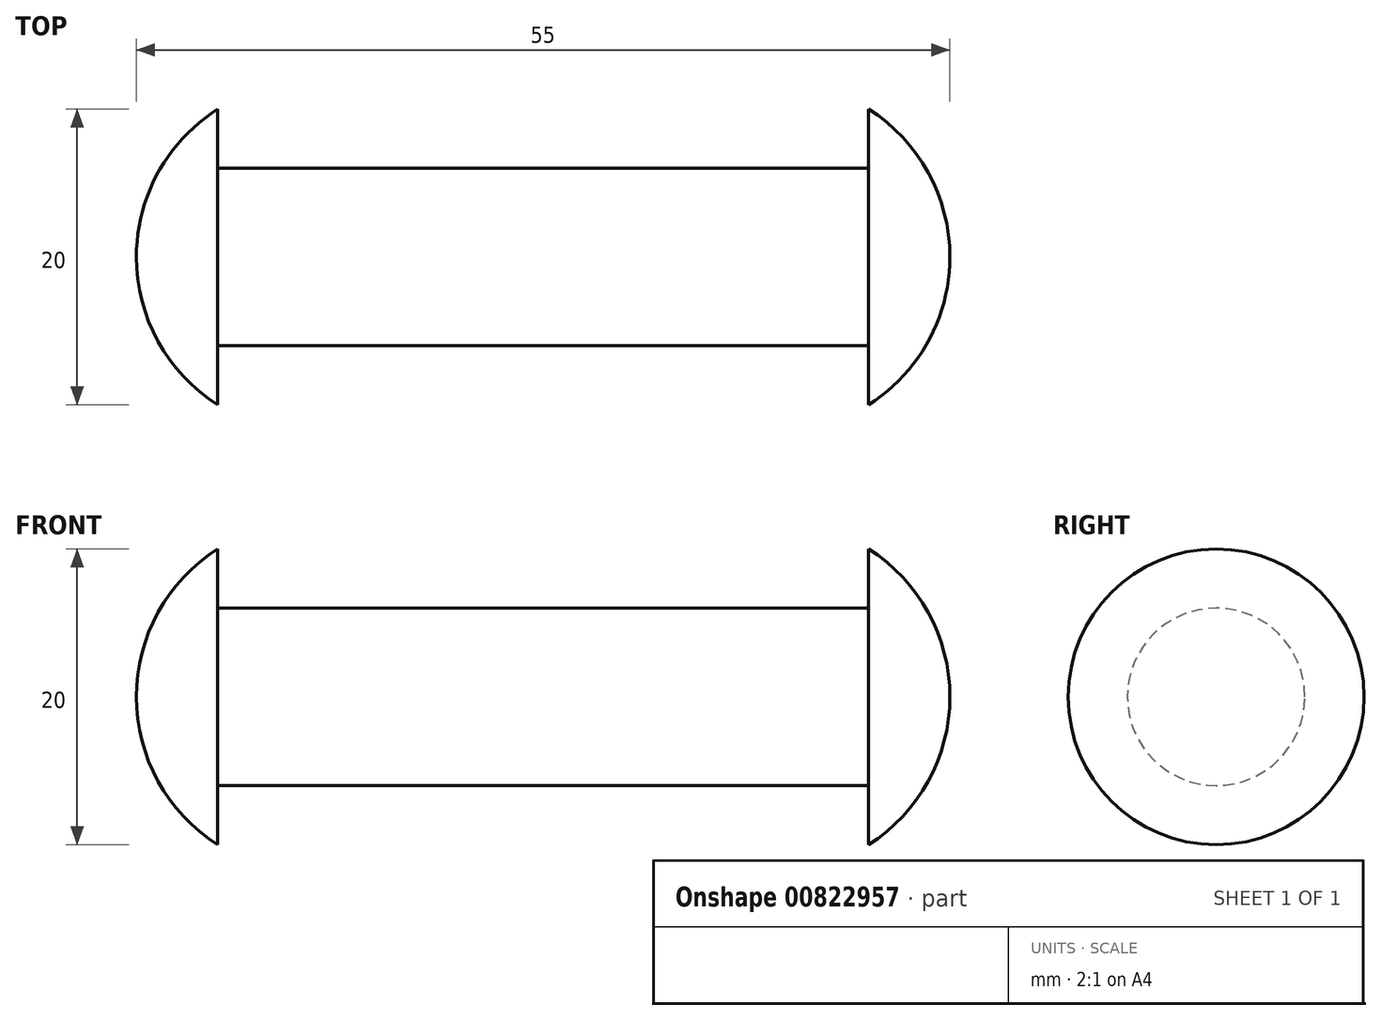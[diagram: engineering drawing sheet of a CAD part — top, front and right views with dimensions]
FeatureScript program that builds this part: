
annotation { "Feature Type Name" : "Feature", "Feature Type Description" : "" }
export const myFeature = defineFeature(function(context is Context, id is Id, definition is map)
    precondition{}
    {
        {
            var Q0;
            Q0=qCreatedBy(makeId("Top.planeOp"),FACE);
            var sketch = newSketch(context, id + "F0", { "sketchPlane" : qUnion([Q0])});
            skLineSegment(sketch, "E0", {"start": v(0, 0) * mm, "end": v(-31.26, 0) * mm, "construction": true});
            skLineSegment(sketch, "E1", {"start": v(0, 0) * mm, "end": v(0, 19.33) * mm, "construction": true});
            skLineSegment(sketch, "E2", {"start": v(0, 6) * mm, "end": v(-22, 6) * mm});
            skLineSegment(sketch, "E3", {"start": v(-22, 6) * mm, "end": v(-22, 10) * mm});
            skLineSegment(sketch, "E4.MirrorCS", {"start": v(-22, -6) * mm, "end": v(-22, -10) * mm, "construction": true});
            skLineSegment(sketch, "E5.MirrorCS", {"start": v(0, -6) * mm, "end": v(-22, -6) * mm, "construction": true});
            skLineSegment(sketch, "E6.MirrorCS", {"start": v(0, 6) * mm, "end": v(22, 6) * mm});
            skLineSegment(sketch, "E7.MirrorCS", {"start": v(22, 6) * mm, "end": v(22, 10) * mm});
            skLineSegment(sketch, "E8.MirrorCS", {"start": v(0, -6) * mm, "end": v(22, -6) * mm, "construction": true});
            skLineSegment(sketch, "E9.MirrorCS", {"start": v(22, -6) * mm, "end": v(22, -10) * mm, "construction": true});
            skArc(sketch, "E10", {"start": v(-22, 10) * mm, "mid": v(-26.03, 5.7) * mm, "end": v(-27.5, 0) * mm});
            skArc(sketch, "E11.MirrorCS", {"start": v(22, 10) * mm, "mid": v(26.03, 5.7) * mm, "end": v(27.5, 0) * mm});
            skLineSegment(sketch, "E12", {"start": v(-27.5, 0) * mm, "end": v(27.5, 0) * mm});
            skPoint(sketch, "E13.orphan", {"position": v(22, -10) * mm});
            skSolve(sketch);
        }
        {
            var Q0;
            Q0 = qSketchRegion(id + "F0", true);
            var Q1;
            Q1=sQuery(id+"F0.wireOp",EDGE,"E0");
            revolve(context, id + "F1", {"surfaceOperationType" : NewSurfaceOperationType.NEW, "entities" : qUnion([Q0]), "axis" : qUnion([Q1]), "revolveType" : RevolveType.FULL});
        }
    });
